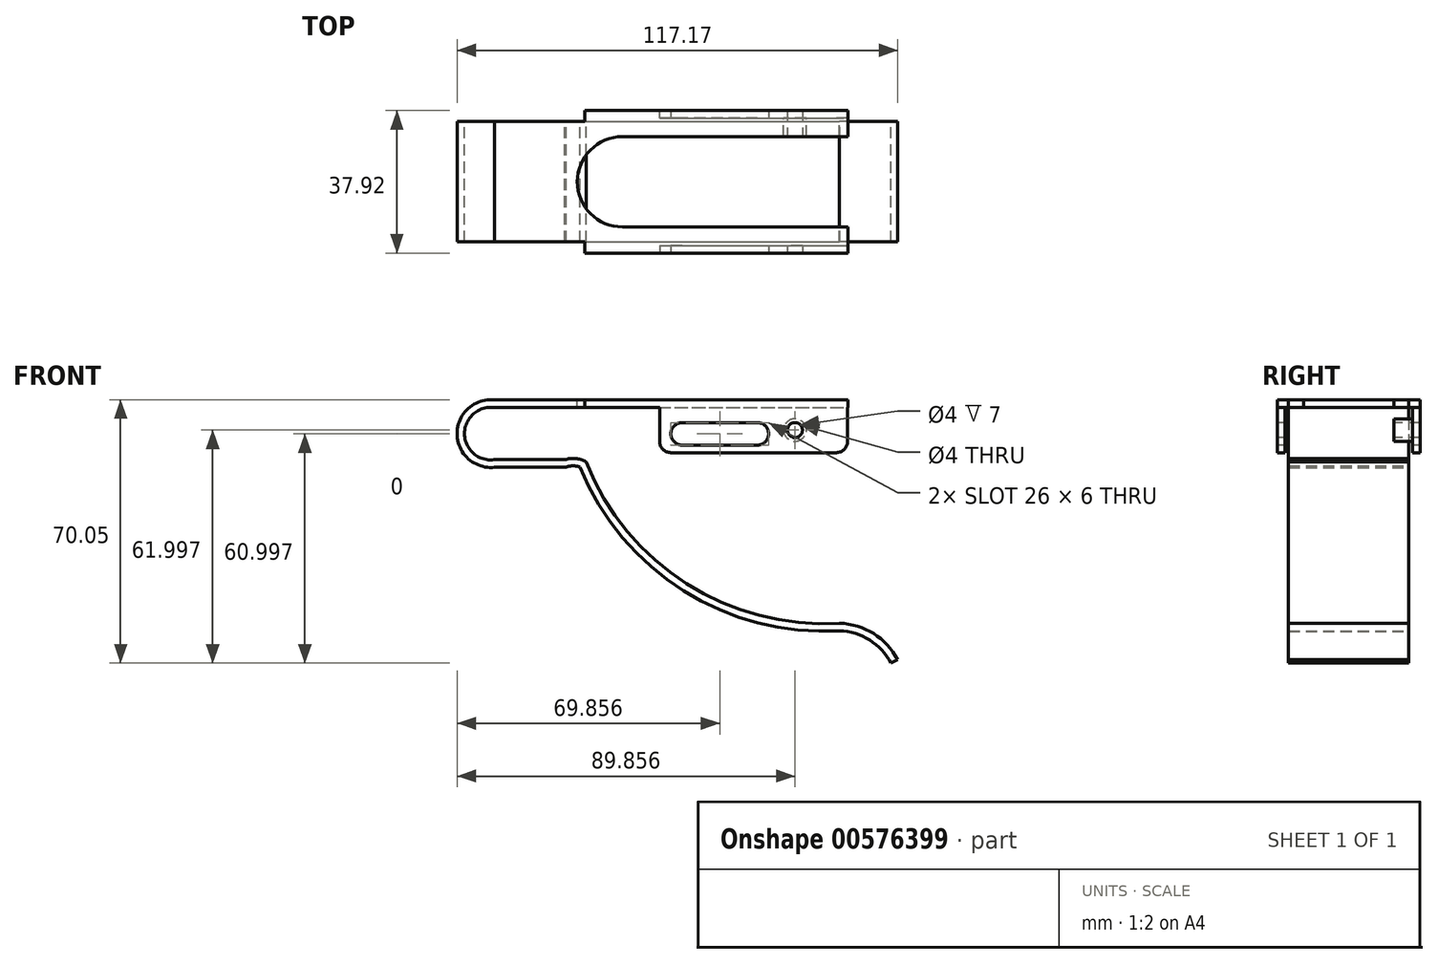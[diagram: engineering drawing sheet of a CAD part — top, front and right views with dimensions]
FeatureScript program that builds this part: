
annotation { "Feature Type Name" : "Feature", "Feature Type Description" : "" }
export const myFeature = defineFeature(function(context is Context, id is Id, definition is map)
    precondition{}
    {
        {
            var Q0;
            Q0=qCreatedBy(makeId("Front.planeOp"),FACE);
            var sketch = newSketch(context, id + "F0", { "sketchPlane" : qUnion([Q0])});
            skArc(sketch, "E0", {"start": v(0, 8.95) * mm, "mid": v(-9.98, 0) * mm, "end": v(0, -8.95) * mm});
            skLineSegment(sketch, "E1", {"start": v(0, 8.95) * mm, "end": v(94, 8.95) * mm});
            skArc(sketch, "E2", {"start": v(22.74, -8.95) * mm, "mid": v(50.26, -41.79) * mm, "end": v(91.77, -52.44) * mm});
            skArc(sketch, "E3", {"start": v(105.41, -61.05) * mm, "mid": v(99.76, -54.9) * mm, "end": v(91.77, -52.44) * mm});
            skLineSegment(sketch, "E4.0", {"start": v(-0.12, 6.95) * mm, "end": v(94, 6.95) * mm});
            skArc(sketch, "E5.0", {"start": v(-0.12, 6.95) * mm, "mid": v(-7.98, 0) * mm, "end": v(-0.12, -6.95) * mm});
            skLineSegment(sketch, "E6", {"start": v(0, -8.95) * mm, "end": v(19, -8.95) * mm});
            skArc(sketch, "E7", {"start": v(22.74, -8.95) * mm, "mid": v(20.87, -8.58) * mm, "end": v(19, -8.95) * mm});
            skLineSegment(sketch, "E8.0", {"start": v(-0.12, -6.95) * mm, "end": v(18.65, -6.95) * mm});
            skArc(sketch, "E9.0", {"start": v(24.31, -7.49) * mm, "mid": v(51.05, -39.92) * mm, "end": v(91.74, -50.44) * mm});
            skArc(sketch, "E10.0", {"start": v(24.31, -7.49) * mm, "mid": v(21.54, -6.61) * mm, "end": v(18.65, -6.95) * mm});
            skArc(sketch, "E11.0", {"start": v(107.19, -60.13) * mm, "mid": v(100.78, -53.18) * mm, "end": v(91.74, -50.44) * mm});
            skLineSegment(sketch, "E12", {"start": v(94, 8.95) * mm, "end": v(94, 6.95) * mm});
            skLineSegment(sketch, "E13", {"start": v(105.41, -61.05) * mm, "end": v(107.19, -60.13) * mm});
            skSolve(sketch);
        }
        {
            var Q0;
            Q0 = qSketchRegion(id + "F0", true);
            extrude(context, id + "F1", {"entities" : qUnion([Q0]), "depth" : 16 * mm, "offsetDistance" : 25 * mm});
        }
        {
            var Q0;
            Q0=makeQuery(id+"F1.opExtrude","SWEPT_FACE",FACE,{"disambiguationData":[OSD([sQuery(id+"F0.wireOp",EDGE,"E1")])]});
            var sketch = newSketch(context, id + "F2", { "sketchPlane" : qUnion([Q0])});
            skLineSegment(sketch, "E14.bottom", {"start": v(23.93, -15.96) * mm, "end": v(93.93, -15.96) * mm});
            skLineSegment(sketch, "E14.top", {"start": v(23.93, -18.96) * mm, "end": v(93.93, -18.96) * mm});
            skLineSegment(sketch, "E14.left", {"start": v(23.93, -15.96) * mm, "end": v(23.93, -18.96) * mm});
            skLineSegment(sketch, "E14.right", {"start": v(93.93, -15.96) * mm, "end": v(93.93, -18.96) * mm});
            skSolve(sketch);
        }
        {
            var Q0;
            Q0 = qSketchRegion(id + "F2", true);
            extrude(context, id + "F3", {"entities" : qUnion([Q0]), "operationType" : NewBodyOperationType.ADD, "oppositeDirection" : true, "depth" : 2 * mm, "offsetDistance" : 25 * mm});
        }
        {
            var Q0;
            Q0=makeQuery(id+"F3.opExtrude","SWEPT_FACE",FACE,{"disambiguationData":[OSD([sQuery(id+"F2.wireOp",EDGE,"E14.top")])]});
            var sketch = newSketch(context, id + "F4", { "sketchPlane" : qUnion([Q0])});
            skLineSegment(sketch, "E15.bottom", {"start": v(43.88, 8.95) * mm, "end": v(93.88, 8.95) * mm});
            skLineSegment(sketch, "E15.top", {"start": v(43.88, -5.05) * mm, "end": v(93.88, -5.05) * mm});
            skLineSegment(sketch, "E15.left", {"start": v(43.88, 8.95) * mm, "end": v(43.88, -5.05) * mm});
            skLineSegment(sketch, "E15.right", {"start": v(93.88, 8.95) * mm, "end": v(93.88, -5.05) * mm});
            skSolve(sketch);
        }
        {
            var Q0;
            Q0 = qSketchRegion(id + "F4", true);
            extrude(context, id + "F5", {"entities" : qUnion([Q0]), "operationType" : NewBodyOperationType.ADD, "oppositeDirection" : true, "depth" : 2 * mm, "offsetDistance" : 25 * mm});
        }
        {
            var Q0;
            Q0=makeQuery(id+"F1.opExtrude","SWEPT_BODY",BODY,{"disambiguationData":[OSD([sQuery(id+"F0.wireOp",EDGE,"E0"),sQuery(id+"F0.wireOp",EDGE,"E1"),sQuery(id+"F0.wireOp",EDGE,"E2"),sQuery(id+"F0.wireOp",EDGE,"E3"),sQuery(id+"F0.wireOp",EDGE,"E4.0"),sQuery(id+"F0.wireOp",EDGE,"E5.0"),sQuery(id+"F0.wireOp",EDGE,"E6"),sQuery(id+"F0.wireOp",EDGE,"E7"),sQuery(id+"F0.wireOp",EDGE,"E8.0"),sQuery(id+"F0.wireOp",EDGE,"E9.0"),sQuery(id+"F0.wireOp",EDGE,"E10.0"),sQuery(id+"F0.wireOp",EDGE,"E11.0"),sQuery(id+"F0.wireOp",EDGE,"E12"),sQuery(id+"F0.wireOp",EDGE,"E13")])]});
            var Q1;
            Q1=qCreatedBy(makeId("Front.planeOp"),FACE);
            mirror(context, id + "F6", {"operationType" : NewBodyOperationType.ADD, "entities" : qUnion([Q0]), "mirrorPlane" : qUnion([Q1])});
        }
        {
            var Q0;
            {var subQ0=makeQuery(id+"F3.boolean.opBoolean","MERGE",FACE,{"derivedFrom":[makeQuery(id+"F1.opExtrude","SWEPT_FACE",FACE,{"disambiguationData":[OSD([sQuery(id+"F0.wireOp",EDGE,"E1")])]}),makeQuery(id+"F3.opExtrude","CAP_FACE",FACE,{"disambiguationData":[OSD([sQuery(id+"F2.wireOp",EDGE,"E14.bottom"),sQuery(id+"F2.wireOp",EDGE,"E14.top"),sQuery(id+"F2.wireOp",EDGE,"E14.left"),sQuery(id+"F2.wireOp",EDGE,"E14.right")])],"isStart":true})]});Q0=makeQuery(id+"F6.boolean.opBoolean","MERGE",FACE,{"derivedFrom":[subQ0,makeQuery(id+"F6.opPattern","COPY",FACE,{"derivedFrom":subQ0,"instanceName":"1"})]});}
            var sketch = newSketch(context, id + "F7", { "sketchPlane" : qUnion([Q0])});
            skArc(sketch, "E16", {"start": v(34, 12) * mm, "mid": v(22, 0) * mm, "end": v(34, -12) * mm});
            skLineSegment(sketch, "E17", {"start": v(34, 12) * mm, "end": v(94, 12) * mm});
            skLineSegment(sketch, "E18", {"start": v(34, -12) * mm, "end": v(94, -12) * mm});
            skLineSegment(sketch, "E19", {"start": v(94, -12) * mm, "end": v(94, 12) * mm});
            skSolve(sketch);
        }
        {
            var Q0;
            Q0 = qSketchRegion(id + "F7", true);
            extrude(context, id + "F8", {"entities" : qUnion([Q0]), "operationType" : NewBodyOperationType.REMOVE, "oppositeDirection" : true, "depth" : 2 * mm, "offsetDistance" : 25 * mm});
        }
        {
            var Q0;
            {var subQ0=sQuery(id+"F4.wireOp",EDGE,"E15.top");Q0=makeQuery(id+"F4.imprint","IMPRINT",FACE,{"disambiguationData":[TD([[makeQuery(id+"F4.imprint","IMPRINT",EDGE,{"derivedFrom":subQ0}),1.0]])]});}
            var sketch = newSketch(context, id + "F9", { "sketchPlane" : qUnion([Q0])});
            skLineSegment(sketch, "E20", {"start": v(49.88, -0.05) * mm, "end": v(69.88, -0.05) * mm});
            skArc(sketch, "E21.0.startCap", {"start": v(49.88, -3.05) * mm, "mid": v(46.88, -0.05) * mm, "end": v(49.88, 2.95) * mm});
            skArc(sketch, "E21.0.endCap", {"start": v(69.88, 2.95) * mm, "mid": v(72.88, -0.05) * mm, "end": v(69.88, -3.05) * mm});
            skLineSegment(sketch, "E21.0.left", {"start": v(49.88, 2.95) * mm, "end": v(69.88, 2.95) * mm});
            skLineSegment(sketch, "E21.0.right", {"start": v(49.88, -3.05) * mm, "end": v(69.88, -3.05) * mm});
            skSolve(sketch);
        }
        {
            var Q0;
            Q0 = qSketchRegion(id + "F9", true);
            extrude(context, id + "F10", {"entities" : qUnion([Q0]), "operationType" : NewBodyOperationType.REMOVE, "endBound" : BoundingType.THROUGH_ALL, "oppositeDirection" : true, "depth" : 25 * mm, "offsetDistance" : 25 * mm});
        }
        {
            var Q0;
            {var subQ0=sQuery(id+"F4.wireOp",EDGE,"E15.top");Q0=makeQuery(id+"F4.imprint","IMPRINT",FACE,{"disambiguationData":[TD([[makeQuery(id+"F4.imprint","IMPRINT",EDGE,{"derivedFrom":subQ0}),1.0]])]});}
            var sketch = newSketch(context, id + "F11", { "sketchPlane" : qUnion([Q0])});
            skPoint(sketch, "E22", {"position": v(79.88, 0.95) * mm});
            skSolve(sketch);
        }
        {
            var Q0;
            Q0=sQuery(id+"F11.wireOp",VERTEX,"E22");
            var Q1;
            Q1=makeQuery(id+"F1.opExtrude","SWEPT_BODY",BODY,{"disambiguationData":[OSD([sQuery(id+"F0.wireOp",EDGE,"E0"),sQuery(id+"F0.wireOp",EDGE,"E1"),sQuery(id+"F0.wireOp",EDGE,"E2"),sQuery(id+"F0.wireOp",EDGE,"E3"),sQuery(id+"F0.wireOp",EDGE,"E4.0"),sQuery(id+"F0.wireOp",EDGE,"E5.0"),sQuery(id+"F0.wireOp",EDGE,"E6"),sQuery(id+"F0.wireOp",EDGE,"E7"),sQuery(id+"F0.wireOp",EDGE,"E8.0"),sQuery(id+"F0.wireOp",EDGE,"E9.0"),sQuery(id+"F0.wireOp",EDGE,"E10.0"),sQuery(id+"F0.wireOp",EDGE,"E11.0"),sQuery(id+"F0.wireOp",EDGE,"E12"),sQuery(id+"F0.wireOp",EDGE,"E13")])]});
            hole(context, id + "F12", {"style" : HoleStyle.SIMPLE, "endStyle" : HoleEndStyle.THROUGH, "holeDiameter" : 4 * mm, "majorDiameter" : 5 * mm, "isTappedThrough" : true, "tappedDepth" : 12 * mm, "tapClearance" : 3, "locations" : qUnion([Q0]), "scope" : qUnion([Q1])});
        }
        {
            var Q0;
            Q0=makeQuery(id+"F6.opPattern","COPY",FACE,{"derivedFrom":makeQuery(id+"F5.opExtrude","CAP_FACE",FACE,{"disambiguationData":[OSD([sQuery(id+"F4.wireOp",EDGE,"E15.bottom"),sQuery(id+"F4.wireOp",EDGE,"E15.top"),sQuery(id+"F4.wireOp",EDGE,"E15.left"),sQuery(id+"F4.wireOp",EDGE,"E15.right")])],"isStart":false}),"instanceName":"1"});
            var sketch = newSketch(context, id + "F13", { "sketchPlane" : qUnion([Q0])});
            skCircle(sketch, "E23.0", {"center": v(79.88, 0.95) * mm, "radius": 2 * mm});
            skCircle(sketch, "E24.0", {"center": v(79.88, 0.95) * mm, "radius": 3 * mm});
            skSolve(sketch);
        }
        {
            var Q0;
            Q0 = qSketchRegion(id + "F13", true);
            extrude(context, id + "F14", {"entities" : qUnion([Q0]), "operationType" : NewBodyOperationType.ADD, "depth" : 5 * mm, "offsetDistance" : 25 * mm});
        }
        {
            var Q0;
            Q0=makeQuery(id+"F5.opExtrude","SWEPT_EDGE",EDGE,{"disambiguationData":[OSD([sQuery(id+"F4.wireOp",EDGE,"E15.top"),sQuery(id+"F4.wireOp",EDGE,"E15.right")])]});
            var Q1;
            Q1=makeQuery(id+"F5.opExtrude","SWEPT_EDGE",EDGE,{"disambiguationData":[OSD([sQuery(id+"F4.wireOp",EDGE,"E15.top"),sQuery(id+"F4.wireOp",EDGE,"E15.left")])]});
            var Q2;
            Q2=makeQuery(id+"F6.opPattern","COPY",EDGE,{"derivedFrom":makeQuery(id+"F5.opExtrude","SWEPT_EDGE",EDGE,{"disambiguationData":[OSD([sQuery(id+"F4.wireOp",EDGE,"E15.top"),sQuery(id+"F4.wireOp",EDGE,"E15.left")])]}),"instanceName":"1"});
            var Q3;
            Q3=makeQuery(id+"F6.opPattern","COPY",EDGE,{"derivedFrom":makeQuery(id+"F5.opExtrude","SWEPT_EDGE",EDGE,{"disambiguationData":[OSD([sQuery(id+"F4.wireOp",EDGE,"E15.top"),sQuery(id+"F4.wireOp",EDGE,"E15.right")])]}),"instanceName":"1"});
            fillet(context, id + "F15", {"entities" : qUnion([Q0, Q1, Q2, Q3]), "radius" : 3 * mm, "tangentPropagation" : true, "allowEdgeOverflow" : false});
        }
    });
